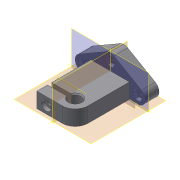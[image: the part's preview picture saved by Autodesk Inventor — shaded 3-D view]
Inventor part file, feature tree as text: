
AUTODESK INVENTOR PART (.ipt)
format: ipt  version: 2015 SP2 (Build 190223200, 223)  size: 300,032 bytes
history: native  units: mm
features: extrude x9, sketch x9, projected_geometry x5, fillet x2, plane x2, other x1, chamfer x1
ambient origin geometry x8: Origin, YZ Plane, XZ Plane, XY Plane, X Axis, Y Axis, Z Axis, Center Point
bodies: Body1 (feature_tree)
feature tree (29):
  other  "Sólido1"
  extrude  "Extrusión1"  Depth=39.25mm
  fillet  "Empalme1"  Radius=11.0mm
  extrude  "Extrusión2"  Depth=3.0mm
  extrude  "Extrusión3"  Depth=1.5mm
  plane  "Plano de trabajo2"
  extrude  "Extrusión5"  Depth=5.244714mm
  extrude  "Extrusión6"  Depth=17.0mm
  extrude  "Extrusión7"  Depth=10.0mm
  extrude  "Extrusión8"  Depth=3.75mm
  plane  "Plano de trabajo3"
  extrude  "Extrusión9"  Depth=6.2mm
  extrude  "Extrusión10"  Depth=4.4mm
  sketch  "Boceto11"  dims[d39=6.2mm d40=6.2mm d41=2.8mm d42=0.0mm d43=7.2mm d44=5.5mm d45=6.8mm d46=2.8mm d47=0.0mm d48=3.75mm d49=26.4mm d50=0.0mm d51=-15.71mm d53=120.0deg d56=6.235mm d57=8.781572mm d58=2.8mm d59=0.0mm d60=2.0mm d61=0.0mm d62=4.4mm d63=9.25mm d64=0.5mm d65=1.0mm d66=2.0mm d67=30.0deg]
  chamfer  "Chamfer1"  Distance=2.8mm
  fillet  "Empalme2"  Radius=7.2mm
  sketch  "Boceto1"  dims[d0=27.75mm d1=39.25mm d2=11.0mm d3=0.0mm]
  projected_geometry  "Contorno proyectado1"
  sketch  "Boceto3"  dims[d4=9.25mm d5=3.0mm]
  sketch  "Boceto5"  dims[d6=7.75mm d13=1.5mm]
  projected_geometry  "Contorno proyectado2"
  sketch  "Boceto6"  dims[d19=11.0mm d20=0.0mm d21=5.244714mm]
  projected_geometry  "Contorno proyectado3"
  sketch  "Boceto7"  dims[d23=39.75mm d25=17.0mm]
  sketch  "Boceto8"  dims[d26=10.0mm d27=0.0mm d33=3.75mm]
  projected_geometry  "Contorno proyectado4"
  sketch  "Boceto9"  dims[d34=3.75mm d35=3.75mm]
  projected_geometry  "Contorno proyectado5"
  sketch  "Boceto10"  dims[d36=2.8mm d37=0.0mm d38=6.2mm]
